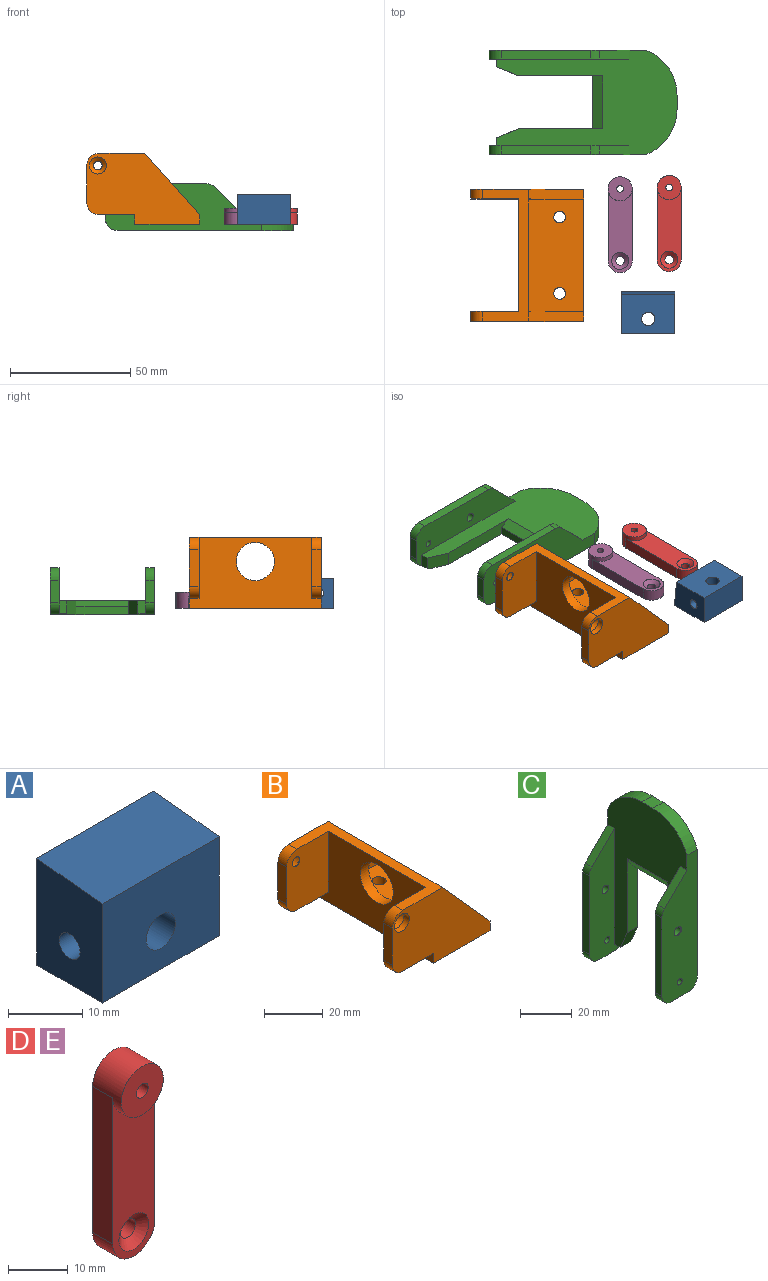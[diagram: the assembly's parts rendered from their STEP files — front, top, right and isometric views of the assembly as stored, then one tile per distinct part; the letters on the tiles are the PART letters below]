
ASSEMBLY  parts=5 mates=3
PART A: 9 faces, bbox 22.2x12.5x17.6 mm
  f0: plane 22.23x16.31mm, normal (0,-1,0), area 338.2mm2, adj f2,f4,f5,f7,f8
  f1: plane 22.23x17.58mm, normal (0,1,0), area 366.5mm2, adj f2,f4,f5,f7,f8
  f2: plane 22.23x12.5mm, normal (0,0,-1), area 277.8mm2, adj f0,f1,f7,f8
  f3: cylinder r=1.98mm len=9.17mm, axis (1,0,0), area 108.9mm2, adj f5,f8
  f4: plane 22.23x12.5mm, normal (0,-0.1,0.99), area 279.2mm2, adj f0,f1,f7,f8
  f5: cylinder r=2.78mm len=12.5mm, axis (0,-1,0), area 191.5mm2, adj f0,f1,f3,f6
  f6: cylinder r=1.98mm len=9.17mm, axis (1,0,0), area 108.9mm2, adj f5,f7
  f7: plane 17.58x12.5mm, normal (1,0,0), area 199.4mm2, adj f0,f1,f2,f4,f6
  f8: plane 17.58x12.5mm, normal (-1,0,0), area 199.4mm2, adj f0,f1,f2,f3,f4
PART B: 31 faces, bbox 47x55.1x29.5 mm
  f0: plane 46.83x22.86mm, normal (0,0,1), area 1033.8mm2, adj f1,f7,f8,f10,f25,f27
  f1: plane 46.83x25.4mm, normal (1,0,0), area 991.4mm2, adj f0,f6,f11,f25,f27
  f2: cone r=3.54mm half-angle=50deg, axis (0,1,0), area 37.8mm2, adj f3,f29
  f3: cylinder r=1.83mm len=3.66mm, axis (0,1,0), area 1.7mm2, adj f2,f13
  f4: cone r=3.54mm half-angle=50deg, axis (0,-1,0), area 37.8mm2, adj f5,f22
  f5: cylinder r=1.83mm len=3.66mm, axis (0,-1,0), area 1.7mm2, adj f4,f15
  f6: cylinder r=7.94mm len=15.88mm, axis (-1,0,0), area 205.8mm2, adj f1,f9
  f7: cylinder r=2.41mm len=4.83mm, axis (0,0,1), area 62.6mm2, adj f0,f24
  f8: cylinder r=2.41mm len=4.83mm, axis (0,0,1), area 62.6mm2, adj f0,f24
  f9: plane 55.08x29.53mm, normal (-1,0,0), area 1218.8mm2, adj f6,f11,f12,f13,f15,f16,f23,f24
  f10: plane 55.08x4.13mm, normal (1,0,0), area 227.3mm2, adj f0,f23,f24,f26,f28,f30
  f11: plane 55.08x19.13mm, normal (0,0,1), area 351.2mm2, adj f1,f9,f13,f15,f20,f21,f23,f26
  f12: plane 15x4.13mm, normal (0,0,-1), area 61.9mm2, adj f9,f13,f19,f30
  f13: plane 25.4x20mm, normal (0,-1,0), area 486.8mm2, adj f3,f9,f11,f12,f14,f19,f20
  f14: plane 15.4x4.13mm, normal (-1,0,0), area 63.6mm2, adj f13,f19,f20,f30
  f15: plane 25.4x20mm, normal (0,1,0), area 486.8mm2, adj f5,f9,f11,f16,f17,f18,f21
  f16: plane 15x4.13mm, normal (0,0,-1), area 61.9mm2, adj f9,f15,f18,f23
  f17: plane 15.4x4.13mm, normal (-1,0,0), area 63.6mm2, adj f15,f18,f21,f23
  f18: cylinder r=5mm len=5mm, axis (0,-1,0), area 32.4mm2, adj f15,f16,f17,f23
  f19: cylinder r=5mm len=5mm, axis (0,1,0), area 32.4mm2, adj f12,f13,f14,f30
  f20: cylinder r=5mm len=5mm, axis (0,-1,0), area 32.4mm2, adj f11,f13,f14,f30
  f21: cylinder r=5mm len=5mm, axis (0,1,0), area 32.4mm2, adj f11,f15,f17,f23
  f22: cylinder r=3.54mm len=7.09mm, axis (0,1,0), area 56.5mm2, adj f4,f23
  f23: plane 46.99x29.53mm, normal (0,-1,0), area 964.4mm2, adj f9,f10,f11,f16,f17,f18,f21,f22
  f24: plane 55.08x26.99mm, normal (0,0,-1), area 1449.9mm2, adj f7,f8,f9,f10,f23,f30
  f25: plane 25.4x22.86mm, normal (0,1,0), area 290.3mm2, adj f0,f1,f26
  f26: plane 25.4x22.86mm, normal (0.74,0,0.67), area 141mm2, adj f10,f11,f23,f25
  f27: plane 25.4x22.86mm, normal (0,-1,0), area 290.3mm2, adj f0,f1,f28
  f28: plane 25.4x22.86mm, normal (0.74,0,0.67), area 141mm2, adj f10,f11,f27,f30
  f29: cylinder r=3.54mm len=7.09mm, axis (0,-1,0), area 56.5mm2, adj f2,f30
  f30: plane 46.99x29.53mm, normal (0,1,0), area 964.4mm2, adj f9,f10,f11,f12,f14,f19,f20,f24
PART C: 35 faces, bbox 19.5x43.5x78.2 mm
  f0: plane 75x43.46mm, normal (-1,0,0), area 1714.5mm2, adj f4,f5,f13,f14,f20,f21,f24,f25
  f1: plane 73.1x43.46mm, normal (1,0,0), area 2184.9mm2, adj f4,f8,f13,f17,f20,f26,f28,f29
  f2: cone r=3.54mm half-angle=50deg, axis (0,-1,0), area 3.2mm2, adj f23,f34
  f3: cylinder r=1.4mm len=3.73mm, axis (0,-1,0), area 32.7mm2, adj f27,f34
  f4: cylinder r=20mm len=18.73mm, axis (-1,0,0), area 138.6mm2, adj f0,f1,f26,f34
  f5: plane 12.24x12.24mm, normal (-0.71,0,0.71), area 64.6mm2, adj f0,f9,f27,f34
  f6: plane 37.26x3.73mm, normal (-1,0,0), area 139mm2, adj f9,f10,f27,f34
  f7: plane 9.29x3.73mm, normal (0,0,-1), area 34.6mm2, adj f8,f10,f27,f34
  f8: cylinder r=5.08mm len=7.74mm, axis (0,1,0), area 36.8mm2, adj f1,f7,f24,f27,f32,f34
  f9: cylinder r=5.08mm len=3.73mm, axis (0,-1,0), area 14.9mm2, adj f5,f6,f27,f34
  f10: cylinder r=5.08mm len=5.08mm, axis (0,-1,0), area 29.8mm2, adj f6,f7,f27,f34
  f11: cone r=3.54mm half-angle=50deg, axis (0,1,0), area 3.2mm2, adj f22,f33
  f12: cylinder r=1.4mm len=3.73mm, axis (0,1,0), area 32.7mm2, adj f25,f33
  f13: cylinder r=20mm len=18.73mm, axis (1,0,0), area 138.6mm2, adj f0,f1,f26,f33
  f14: plane 12.24x12.24mm, normal (-0.71,0,0.71), area 64.6mm2, adj f0,f19,f25,f33
  f15: plane 37.26x3.73mm, normal (-1,0,0), area 139mm2, adj f18,f19,f25,f33
  f16: plane 9.29x3.73mm, normal (0,0,-1), area 34.6mm2, adj f17,f18,f25,f33
  f17: cylinder r=5.08mm len=7.74mm, axis (0,-1,0), area 36.8mm2, adj f1,f16,f21,f25,f31,f33
  f18: cylinder r=5.08mm len=5.08mm, axis (0,1,0), area 29.8mm2, adj f15,f16,f25,f33
  f19: cylinder r=5.08mm len=3.73mm, axis (0,1,0), area 14.9mm2, adj f14,f15,f25,f33
  f20: plane 35.11x5.72mm, normal (0,1,0), area 182.4mm2, adj f0,f1,f28,f30,f32
  f21: plane 5.34x3.19mm, normal (0,0,-1), area 17mm2, adj f0,f17,f25,f31
  f22: cylinder r=1.83mm len=3.66mm, axis (0,1,0), area 40.9mm2, adj f11,f25
  f23: cylinder r=1.83mm len=3.66mm, axis (0,-1,0), area 40.9mm2, adj f2,f27
  f24: plane 5.34x3.19mm, normal (0,0,-1), area 17mm2, adj f0,f8,f27,f32
  f25: plane 58.18x19.08mm, normal (0,-1,0), area 694.6mm2, adj f0,f12,f14,f15,f16,f17,f18,f19
  f26: plane 6x5.72mm, normal (0,0,1), area 34.3mm2, adj f0,f1,f4,f13
  f27: plane 58.18x19.08mm, normal (0,1,0), area 694.6mm2, adj f0,f3,f5,f6,f7,f8,f9,f10
  f28: plane 22x3.41mm, normal (0,0,-1), area 74.9mm2, adj f1,f20,f29,f30
  f29: plane 35.11x5.72mm, normal (0,-1,0), area 182.4mm2, adj f0,f1,f28,f30,f31
  f30: plane 22x4mm, normal (-0.87,0,-0.5), area 101.6mm2, adj f0,f20,f28,f29
  f31: plane 8.91x5.73mm, normal (0,-0.92,-0.39), area 55mm2, adj f0,f1,f17,f21,f29
  f32: plane 8.91x5.73mm, normal (0,0.92,-0.39), area 55mm2, adj f0,f1,f8,f20,f24
  f33: plane 65.19x19.45mm, normal (0,1,0), area 1046.4mm2, adj f0,f1,f11,f12,f13,f14,f15,f16
  f34: plane 65.19x19.45mm, normal (0,-1,0), area 1046.4mm2, adj f0,f1,f2,f3,f4,f5,f6,f7
PART D: 10 faces, bbox 10x6.8x40 mm
  f0: cone r=3.54mm half-angle=50deg, axis (0,-1,0), area 37.8mm2, adj f1,f4
  f1: cylinder r=1.83mm len=3.66mm, axis (0,-1,0), area 38.2mm2, adj f0,f9
  f2: cylinder r=1.4mm len=6.76mm, axis (0,1,0), area 59.4mm2, adj f8,f9
  f3: cylinder r=5mm len=10mm, axis (0,1,0), area 137.6mm2, adj f4,f6,f7,f8,f9
  f4: plane 35x10mm, normal (0,-1,0), area 260.6mm2, adj f0,f3,f5,f6,f7
  f5: cylinder r=5mm len=10mm, axis (0,1,0), area 74.8mm2, adj f4,f6,f7,f9
  f6: plane 30x4.76mm, normal (1,0,0), area 142.9mm2, adj f3,f4,f5,f9
  f7: plane 30x4.76mm, normal (-1,0,0), area 142.9mm2, adj f3,f4,f5,f9
  f8: plane 10x10mm, normal (0,-1,0), area 72.4mm2, adj f2,f3
  f9: plane 40x10mm, normal (0,1,0), area 361.9mm2, adj f1,f2,f3,f5,f6,f7
PART E: same geometry as D
PLACE A rot(axis=(-1,0,0),90deg) t=(53.87,-51.47,-2.54)mm
PLACE B at identity fixed
PLACE C rot(axis=(0,1,0),90deg) t=(-27.13,61.7,-15.78)mm
PLACE D rot(axis=(-1,0,0),90deg) t=(62.61,-26.8,-0.95)mm
PLACE E rot(axis=(-1,0,0),90deg) t=(42.17,-27.3,-0.95)mm
MATE planar B.f24 <-> E.f9  axis (0,0,-1) through (13.41,-25,-2.54)mm
MATE planar B.f24 <-> D.f9  axis (0,0,-1) through (13.41,-25,-2.54)mm
MATE planar A.f1 <-> B.f24  axis (0,0,-1) through (53.87,-48.76,-2.54)mm
